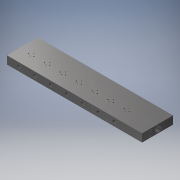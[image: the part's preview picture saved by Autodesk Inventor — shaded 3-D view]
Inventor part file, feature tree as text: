
AUTODESK INVENTOR PART (.ipt)
format: ipt  version: 2018 (Build 220112000, 112)  size: 286,720 bytes
history: native  units: mm
features: hole x8, pattern_linear x2, sketch x2, extrude x1, thread x1
ambient origin geometry x8: Origin, YZ Plane, XZ Plane, XY Plane, X Axis, Y Axis, Z Axis, Center Point
bodies: Volumenkörper1 (feature_tree)
feature tree (14):
  extrude  "Extrusion1"  Depth=170.0mm
  hole  "Bohrung1"  [1 undecoded]
  hole  "Bohrung2"  [1 undecoded]
  pattern_linear  "Rechteckige Anordnung1"  Spacing1=5.0mm  [1 undecoded]
  hole  "Bohrung5"  [1 undecoded]
  hole  "Bohrung6"  [1 undecoded]
  pattern_linear  "Rechteckige Anordnung2"  Spacing1=2.0mm  [1 undecoded]
  hole  "Bohrung14"  [1 undecoded]
  hole  "Bohrung15"  [1 undecoded]
  hole  "Bohrung16"  [1 undecoded]
  hole  "Bohrung17"  [1 undecoded]
  thread  "Thread1"  [1 undecoded]
  sketch  "Skizze2"  dims[d0=39.0mm d1=170.0mm]
  sketch  "Skizze10"  dims[d2=10.0mm d3=0.0mm d6=10.0mm d7=27.0mm d8=5.0mm d9=10.0mm d10=3.8mm d11=2.0mm d12=5.0mm d13=1.2mm d14=6.0mm d15=4.0mm d16=2.0mm d17=90.0deg d18=5.0mm d19=20.594885mm d20=3.25mm d21=3.25mm d22=1.7mm d23=1.7mm d24=1.221mm d25=5.0mm d26=4.0mm d27=2.0mm d28=90.0deg d29=7.0mm d30=20.594885mm d41=70.0mm d43=20.0mm d53=15.0mm d54=5.0mm d55=2.0mm d56=6.0mm d57=4.0mm d58=2.0mm d59=90.0deg d60=14.0mm d61=20.594885mm d73=10.0mm d74=10.0mm d64=4.134mm d65=6.0mm d66=4.0mm d67=2.0mm d68=90.0deg d69=7.0mm d70=20.594885mm d71=70.0mm d75=20.0mm d145=28.0mm d146=28.0mm d147=2.0mm d148=2.0mm d149=2.459mm d150=10.0mm d151=4.0mm d152=2.0mm d153=90.0deg d154=12.0mm d155=20.594885mm d156=2.459mm d157=10.0mm d158=4.0mm d159=2.0mm d160=90.0deg d161=12.0mm d162=20.594885mm d163=18.0mm d164=8.0mm d165=8.0mm d166=10.0mm d167=4.0mm d168=2.0mm d169=90.0deg d170=166.0mm d171=135.0deg d172=10.0mm d173=10.0mm d174=8.6mm d175=10.0mm d176=4.0mm d177=2.0mm d178=90.0deg d179=12.0mm d180=135.0deg d181=10.0mm d182=0.0mm]
note: 11 required parameter values undecoded (feature->parameter linkage not recoverable at this tier; creation-order binding heuristic only, values carry confidence <= 0.55)
